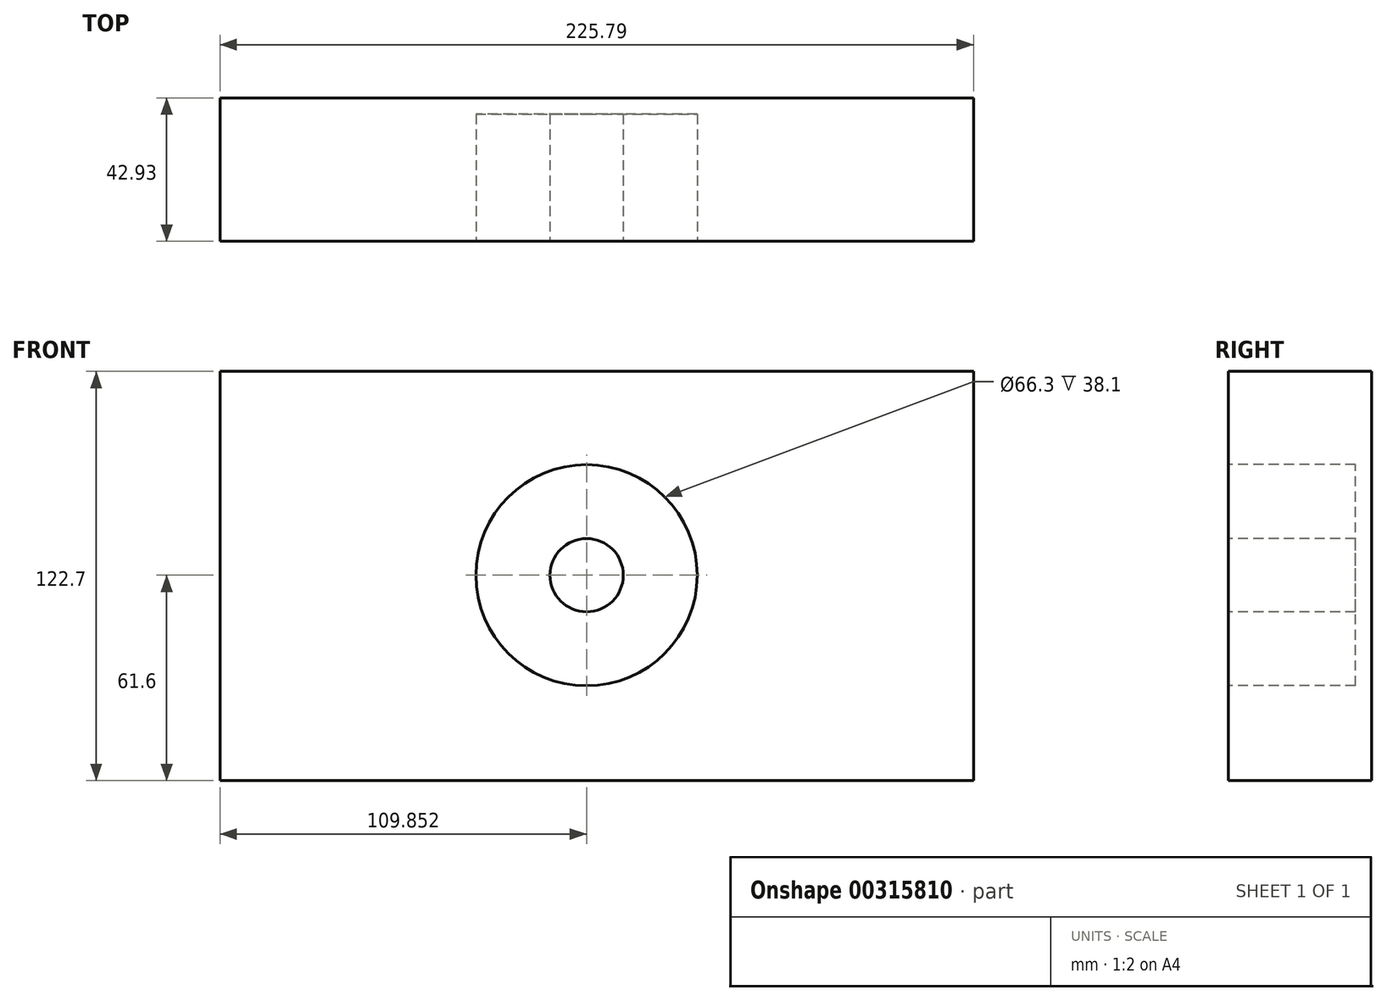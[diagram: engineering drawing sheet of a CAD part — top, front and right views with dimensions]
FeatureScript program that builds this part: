
annotation { "Feature Type Name" : "Feature", "Feature Type Description" : "" }
export const myFeature = defineFeature(function(context is Context, id is Id, definition is map)
    precondition{}
    {
        {
            var Q0;
            Q0=qCreatedBy(makeId("Front.planeOp"),FACE);
            var sketch = newSketch(context, id + "F0", { "sketchPlane" : qUnion([Q0])});
            skLineSegment(sketch, "E0.bottom", {"start": v(-131.85, 61.1) * mm, "end": v(93.94, 61.1) * mm});
            skLineSegment(sketch, "E0.top", {"start": v(-131.85, -61.6) * mm, "end": v(93.94, -61.6) * mm});
            skLineSegment(sketch, "E0.left", {"start": v(-131.85, 61.1) * mm, "end": v(-131.85, -61.6) * mm});
            skLineSegment(sketch, "E0.right", {"start": v(93.94, 61.1) * mm, "end": v(93.94, -61.6) * mm});
            skSolve(sketch);
        }
        {
            var Q0;
            Q0=makeQuery(id+"F0.imprint","IMPRINT",FACE,{"disambiguationData":[TD([[makeQuery(id+"F0.imprint","IMPRINT",EDGE,{"derivedFrom":sQuery(id+"F0.wireOp",EDGE,"E0.bottom")}),-1.0]])]});
            extrude(context, id + "F1", {"entities" : qUnion([Q0]), "depth" : 42.93 * mm});
        }
        {
            var Q0;
            Q0=makeQuery(id+"F1.opExtrude","CAP_FACE",FACE,{"disambiguationData":[OSD([sQuery(id+"F0.wireOp",EDGE,"E0.bottom"),sQuery(id+"F0.wireOp",EDGE,"E0.top"),sQuery(id+"F0.wireOp",EDGE,"E0.left"),sQuery(id+"F0.wireOp",EDGE,"E0.right")])],"isStart":false});
            var sketch = newSketch(context, id + "F2", { "sketchPlane" : qUnion([Q0])});
            skCircle(sketch, "E1", {"center": v(-22, 0) * mm, "radius": 33.15 * mm});
            skCircle(sketch, "E2", {"center": v(-22, 0) * mm, "radius": 10.99 * mm});
            skSolve(sketch);
        }
        {
            var Q0;
            Q0=makeQuery(id+"F2.imprint","IMPRINT",FACE,{"disambiguationData":[TD([[makeQuery(id+"F2.imprint","IMPRINT",EDGE,{"derivedFrom":sQuery(id+"F2.wireOp",EDGE,"E1")}),1.0]])]});
            var Q1;
            Q1=sQuery(id+"F2.wireOp",EDGE,"E2");
            var Q2;
            Q2=sQuery(id+"F2.wireOp",EDGE,"E1");
            extrude(context, id + "F3", {"entities" : qUnion([Q0]), "operationType" : NewBodyOperationType.REMOVE, "surfaceEntities" : qUnion([Q1, Q2]), "endBound" : BoundingType.SYMMETRIC, "oppositeDirection" : true, "depth" : 76.2 * mm});
        }
    });
